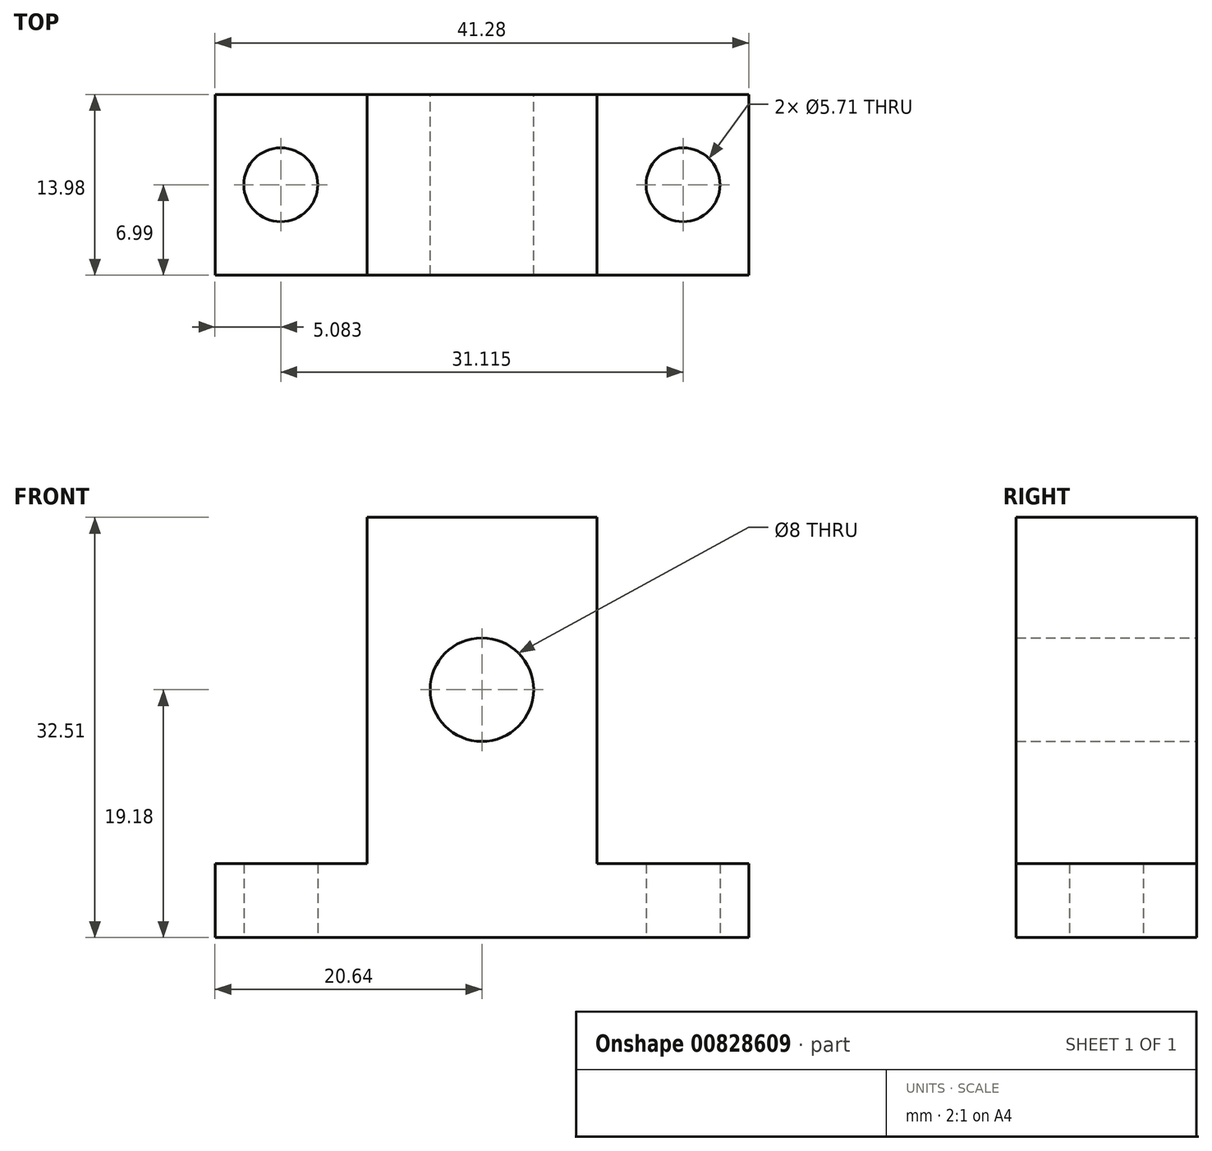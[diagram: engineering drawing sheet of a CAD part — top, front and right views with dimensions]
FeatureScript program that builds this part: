
annotation { "Feature Type Name" : "Feature", "Feature Type Description" : "" }
export const myFeature = defineFeature(function(context is Context, id is Id, definition is map)
    precondition{}
    {
        {
            var Q0;
            Q0=qCreatedBy(makeId("Front.planeOp"),FACE);
            var sketch = newSketch(context, id + "F0", { "sketchPlane" : qUnion([Q0])});
            skLineSegment(sketch, "E0.bottom", {"start": v(-8.9, 13.34) * mm, "end": v(8.9, 13.34) * mm});
            skLineSegment(sketch, "E0.left", {"start": v(-8.9, 13.33) * mm, "end": v(-8.9, -13.46) * mm});
            skLineSegment(sketch, "E0.right", {"start": v(8.9, 13.34) * mm, "end": v(8.9, -13.46) * mm});
            skLineSegment(sketch, "E1.bottom", {"start": v(-20.64, -13.46) * mm, "end": v(-8.9, -13.46) * mm});
            skLineSegment(sketch, "E1.top", {"start": v(-20.64, -19.18) * mm, "end": v(20.64, -19.18) * mm});
            skLineSegment(sketch, "E1.left", {"start": v(-20.64, -13.46) * mm, "end": v(-20.64, -19.18) * mm});
            skLineSegment(sketch, "E1.right", {"start": v(20.64, -13.46) * mm, "end": v(20.64, -19.18) * mm});
            skLineSegment(sketch, "E2.trimOffspring", {"start": v(8.9, -13.46) * mm, "end": v(20.64, -13.46) * mm});
            skCircle(sketch, "E3", {"center": v(0, 0) * mm, "radius": 4 * mm});
            skSolve(sketch);
        }
        {
            var Q0;
            Q0=makeQuery(id+"F0.imprint","IMPRINT",FACE,{"disambiguationData":[TD([[makeQuery(id+"F0.imprint","IMPRINT",EDGE,{"derivedFrom":sQuery(id+"F0.wireOp",EDGE,"E0.bottom")}),-1.0]])]});
            extrude(context, id + "F1", {"entities" : qUnion([Q0]), "endBound" : BoundingType.SYMMETRIC, "depth" : 13.97 * mm, "offsetDistance" : 25.4 * mm});
        }
        {
            var Q0;
            Q0=makeQuery(id+"F1.opExtrude","SWEPT_FACE",FACE,{"disambiguationData":[OSD([sQuery(id+"F0.wireOp",EDGE,"E1.top")])]});
            var sketch = newSketch(context, id + "F2", { "sketchPlane" : qUnion([Q0])});
            skCircle(sketch, "E4", {"center": v(-15.56, 0) * mm, "radius": 2.86 * mm});
            skCircle(sketch, "E5", {"center": v(15.56, 0) * mm, "radius": 2.86 * mm});
            skSolve(sketch);
        }
        {
            var Q0;
            Q0=makeQuery(id+"F2.imprint","IMPRINT",FACE,{"disambiguationData":[TD([[makeQuery(id+"F2.imprint","IMPRINT",EDGE,{"derivedFrom":sQuery(id+"F2.wireOp",EDGE,"E4")}),1.0]])]});
            var Q1;
            Q1=makeQuery(id+"F2.imprint","IMPRINT",FACE,{"disambiguationData":[TD([[makeQuery(id+"F2.imprint","IMPRINT",EDGE,{"derivedFrom":sQuery(id+"F2.wireOp",EDGE,"E5")}),1.0]])]});
            extrude(context, id + "F3", {"entities" : qUnion([Q0, Q1]), "operationType" : NewBodyOperationType.REMOVE, "endBound" : BoundingType.UP_TO_NEXT, "oppositeDirection" : true, "depth" : 25.4 * mm, "offsetDistance" : 25.4 * mm});
        }
    });
